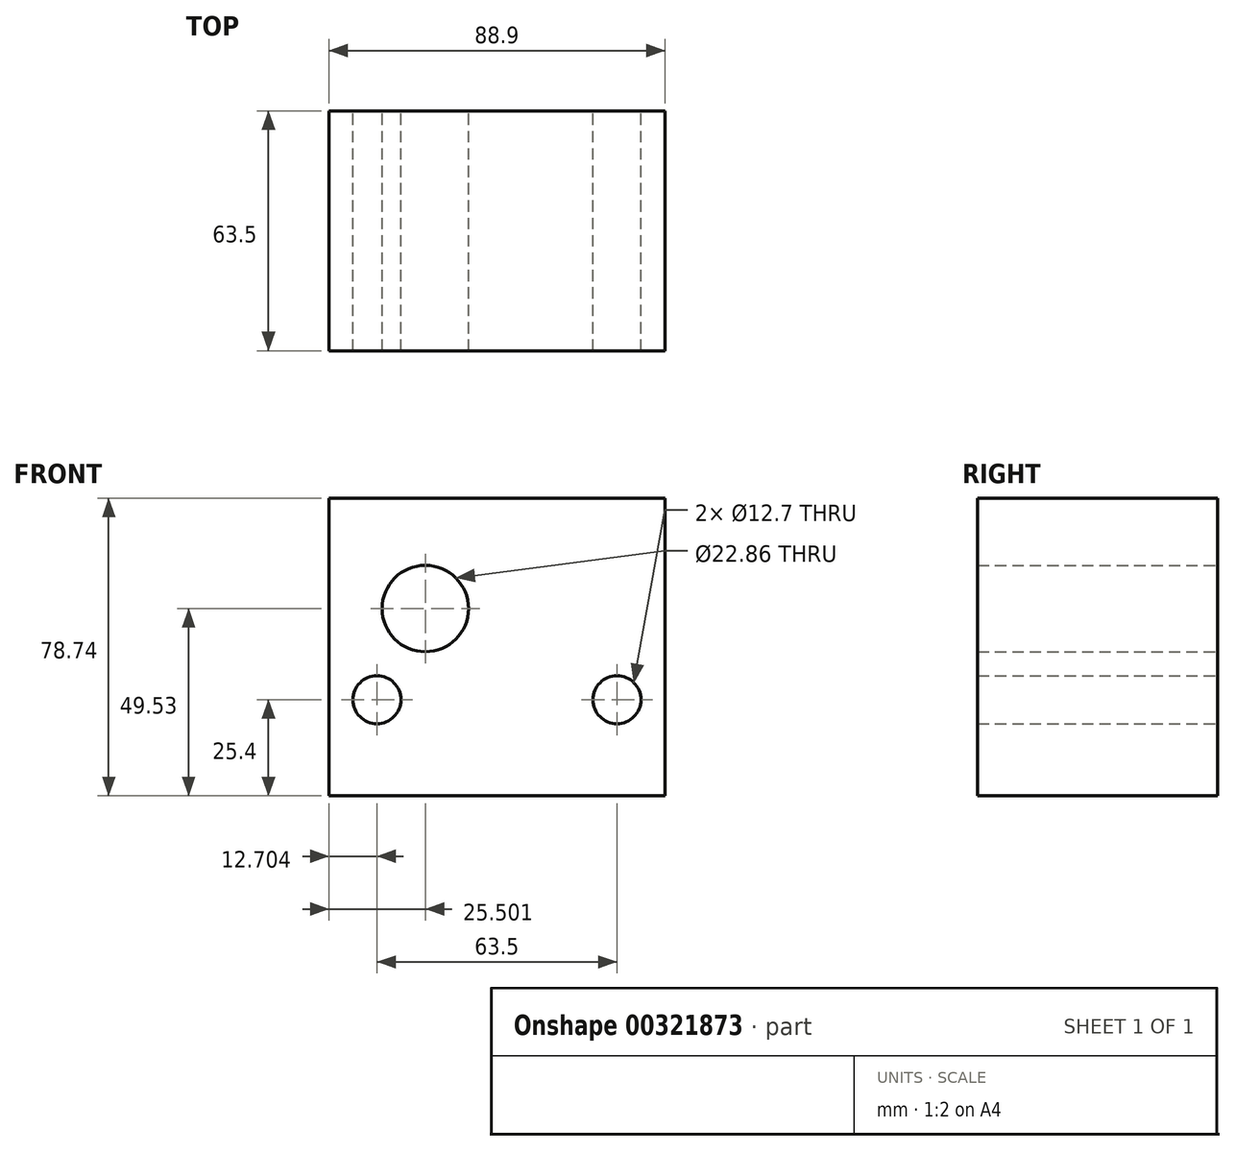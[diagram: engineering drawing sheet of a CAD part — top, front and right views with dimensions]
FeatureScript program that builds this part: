
annotation { "Feature Type Name" : "Feature", "Feature Type Description" : "" }
export const myFeature = defineFeature(function(context is Context, id is Id, definition is map)
    precondition{}
    {
        {
            var Q0;
            Q0=qCreatedBy(makeId("Front.planeOp"),FACE);
            var sketch = newSketch(context, id + "F0", { "sketchPlane" : qUnion([Q0])});
            skLineSegment(sketch, "E0.bottom", {"start": v(-48.65, 45.03) * mm, "end": v(40.25, 45.03) * mm});
            skLineSegment(sketch, "E0.top", {"start": v(-48.65, -33.71) * mm, "end": v(40.25, -33.71) * mm});
            skLineSegment(sketch, "E0.left", {"start": v(-48.65, 45.03) * mm, "end": v(-48.65, -33.71) * mm});
            skLineSegment(sketch, "E0.right", {"start": v(40.25, 45.03) * mm, "end": v(40.25, -33.71) * mm});
            skCircle(sketch, "E1", {"center": v(-23.15, 15.82) * mm, "radius": 11.43 * mm});
            skCircle(sketch, "E2", {"center": v(-35.95, -8.31) * mm, "radius": 6.35 * mm});
            skCircle(sketch, "E3", {"center": v(27.55, -8.31) * mm, "radius": 6.35 * mm});
            skSolve(sketch);
        }
        {
            var Q0;
            Q0 = qSketchRegion(id + "F0", true);
            extrude(context, id + "F1", {"entities" : qUnion([Q0]), "endBound" : BoundingType.SYMMETRIC, "depth" : 63.5 * mm});
        }
    });
